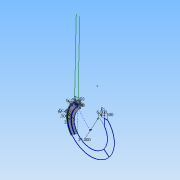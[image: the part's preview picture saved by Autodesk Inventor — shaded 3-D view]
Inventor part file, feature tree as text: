
AUTODESK INVENTOR PART (.ipt)
format: ipt  version: 2013 (Build 170138000, 138)  size: 164,864 bytes
history: native  units: in
note: dims shown in document units (in); Inventor stores cm internally (conversion verified against a paired STEP export)
features: reference x3, extrude x2, plane x1, other x1, sketch x1
ambient origin geometry x8: Origin, YZ Plane, XZ Plane, XY Plane, X Axis, Y Axis, Z Axis, Center Point
bodies: Solid3 (feature_tree)
feature tree (8):
  plane  "Work Plane1"
  extrude  "Extrusion6"  Depth=2.5in
  extrude  "Extrusion7"  Depth=33.0in
  other  "ThermoBulbBorder"
  reference  "Reference2"
  reference  "Reference3"
  reference  "Reference4"
  sketch  "Sketch3"  dims[d0=24.0in d5=2.5in d6=2.5in d7=33.0in d8=0.48in d9=0.48in d10=2.25in d11=1.61in d12=6.0in d20=0.5in d38=0.48in d39=2.25in d53=4.25in d54=0.71in d55=0.0in d56=0.5in d57=0.48in d58=2.25in d60=0.48in d61=2.5in d62=0.25in d63=0.48in d64=0.76in d65=1.24in d66=0.76in d67=1.24in d68=2.25in d69=0.48in d70=0.5in d71=0.0in]
